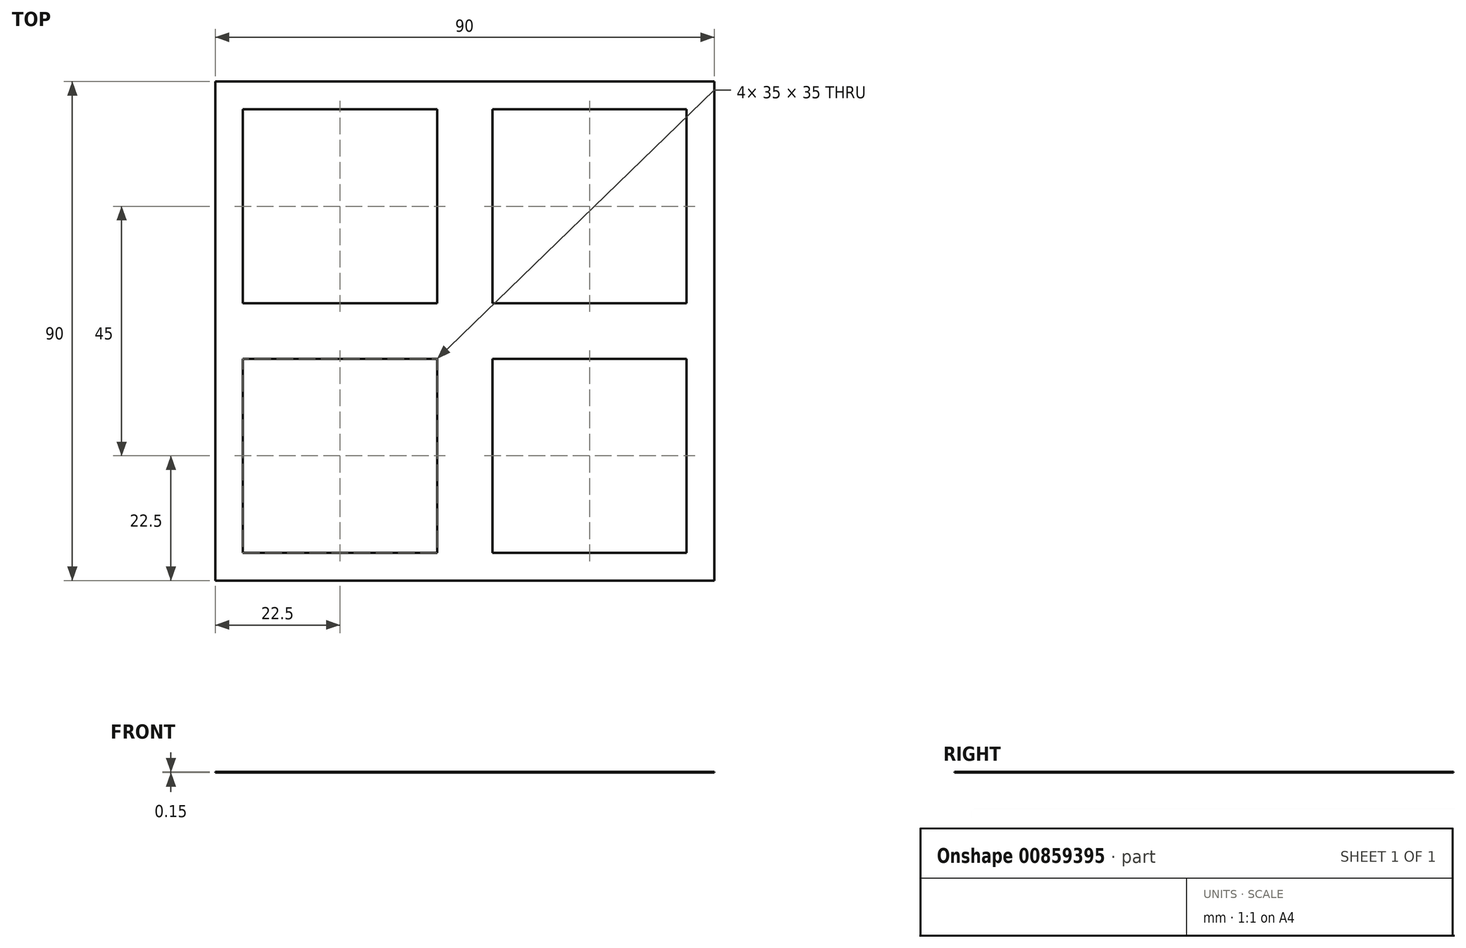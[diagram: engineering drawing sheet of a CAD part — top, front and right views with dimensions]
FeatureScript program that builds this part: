
annotation { "Feature Type Name" : "Feature", "Feature Type Description" : "" }
export const myFeature = defineFeature(function(context is Context, id is Id, definition is map)
    precondition{}
    {
        {
            var Q0;
            Q0=qCreatedBy(makeId("Top.planeOp"),FACE);
            var sketch = newSketch(context, id + "F0", { "sketchPlane" : qUnion([Q0])});
            skLineSegment(sketch, "E0.bottom", {"start": v(45, 45) * mm, "end": v(-45, 45) * mm});
            skLineSegment(sketch, "E0.top", {"start": v(45, -45) * mm, "end": v(-45, -45) * mm});
            skLineSegment(sketch, "E0.left", {"start": v(45, 45) * mm, "end": v(45, -45) * mm});
            skLineSegment(sketch, "E0.right", {"start": v(-45, 45) * mm, "end": v(-45, -45) * mm});
            skPoint(sketch, "E0.middle", {"position": v(0, 0) * mm});
            skLineSegment(sketch, "E1.bottom", {"start": v(5, 40) * mm, "end": v(40, 40) * mm});
            skLineSegment(sketch, "E1.top", {"start": v(5, 5) * mm, "end": v(40, 5) * mm});
            skLineSegment(sketch, "E1.left", {"start": v(5, 40) * mm, "end": v(5, 5) * mm});
            skLineSegment(sketch, "E1.right", {"start": v(40, 40) * mm, "end": v(40, 5) * mm});
            skLineSegment(sketch, "E2.MirrorCS", {"start": v(-5, 40) * mm, "end": v(-40, 40) * mm});
            skLineSegment(sketch, "E3.MirrorCS", {"start": v(-40, 40) * mm, "end": v(-40, 5) * mm});
            skLineSegment(sketch, "E4.MirrorCS", {"start": v(-5, 5) * mm, "end": v(-40, 5) * mm});
            skLineSegment(sketch, "E5.MirrorCS", {"start": v(-5, 40) * mm, "end": v(-5, 5) * mm});
            skLineSegment(sketch, "E6.MirrorCS", {"start": v(-5, -5) * mm, "end": v(-40, -5) * mm});
            skLineSegment(sketch, "E7.MirrorCS", {"start": v(-40, -40) * mm, "end": v(-40, -5) * mm});
            skLineSegment(sketch, "E8.MirrorCS", {"start": v(-5, -40) * mm, "end": v(-5, -5) * mm});
            skLineSegment(sketch, "E9.MirrorCS", {"start": v(5, -40) * mm, "end": v(5, -5) * mm});
            skLineSegment(sketch, "E10.MirrorCS", {"start": v(-5, -40) * mm, "end": v(-40, -40) * mm});
            skLineSegment(sketch, "E11.MirrorCS", {"start": v(40, -40) * mm, "end": v(40, -5) * mm});
            skLineSegment(sketch, "E12.MirrorCS", {"start": v(5, -40) * mm, "end": v(40, -40) * mm});
            skLineSegment(sketch, "E13.MirrorCS", {"start": v(5, -5) * mm, "end": v(40, -5) * mm});
            skSolve(sketch);
        }
        {
            var Q0;
            Q0=makeQuery(id+"F0.imprint","IMPRINT",FACE,{"disambiguationData":[TD([[makeQuery(id+"F0.imprint","IMPRINT",EDGE,{"derivedFrom":sQuery(id+"F0.wireOp",EDGE,"E0.bottom")}),1.0]])]});
            extrude(context, id + "F1", {"entities" : qUnion([Q0]), "flatOperationType" : FlatOperationType.REMOVE, "depth" : .15 * mm, "offsetDistance" : 25 * mm, "domain" : OperationDomain.MODEL});
        }
    });
